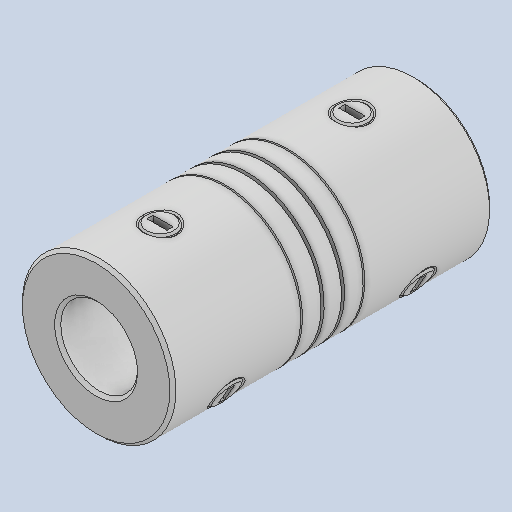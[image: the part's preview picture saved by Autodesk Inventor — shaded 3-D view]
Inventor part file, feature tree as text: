
AUTODESK INVENTOR PART (.ipt)
format: ipt  version: 2023 (Build 270158000, 158)  size: 337,408 bytes
history: native  units: mm
features: mirror x2, pattern_circular x1, boolean_combine x1, chamfer x1
ambient origin geometry x8: Origin, YZ Plane, XZ Plane, XY Plane, X Axis, Y Axis, Z Axis, Center Point
bodies: Solid1 (feature_tree), Solid2 (feature_tree), Solid3 (feature_tree), Solid4 (feature_tree), Solid5 (feature_tree)
feature tree (5):
  mirror  "Mirror1[2]"
  pattern_circular  "CirPattern3"
  mirror  "Mirror1[3]"
  boolean_combine  "Combine1"
  chamfer  "Chamfer2"  [1 undecoded]
note: 1 required parameter value undecoded (feature->parameter linkage not recoverable at this tier; creation-order binding heuristic only, values carry confidence <= 0.55)
